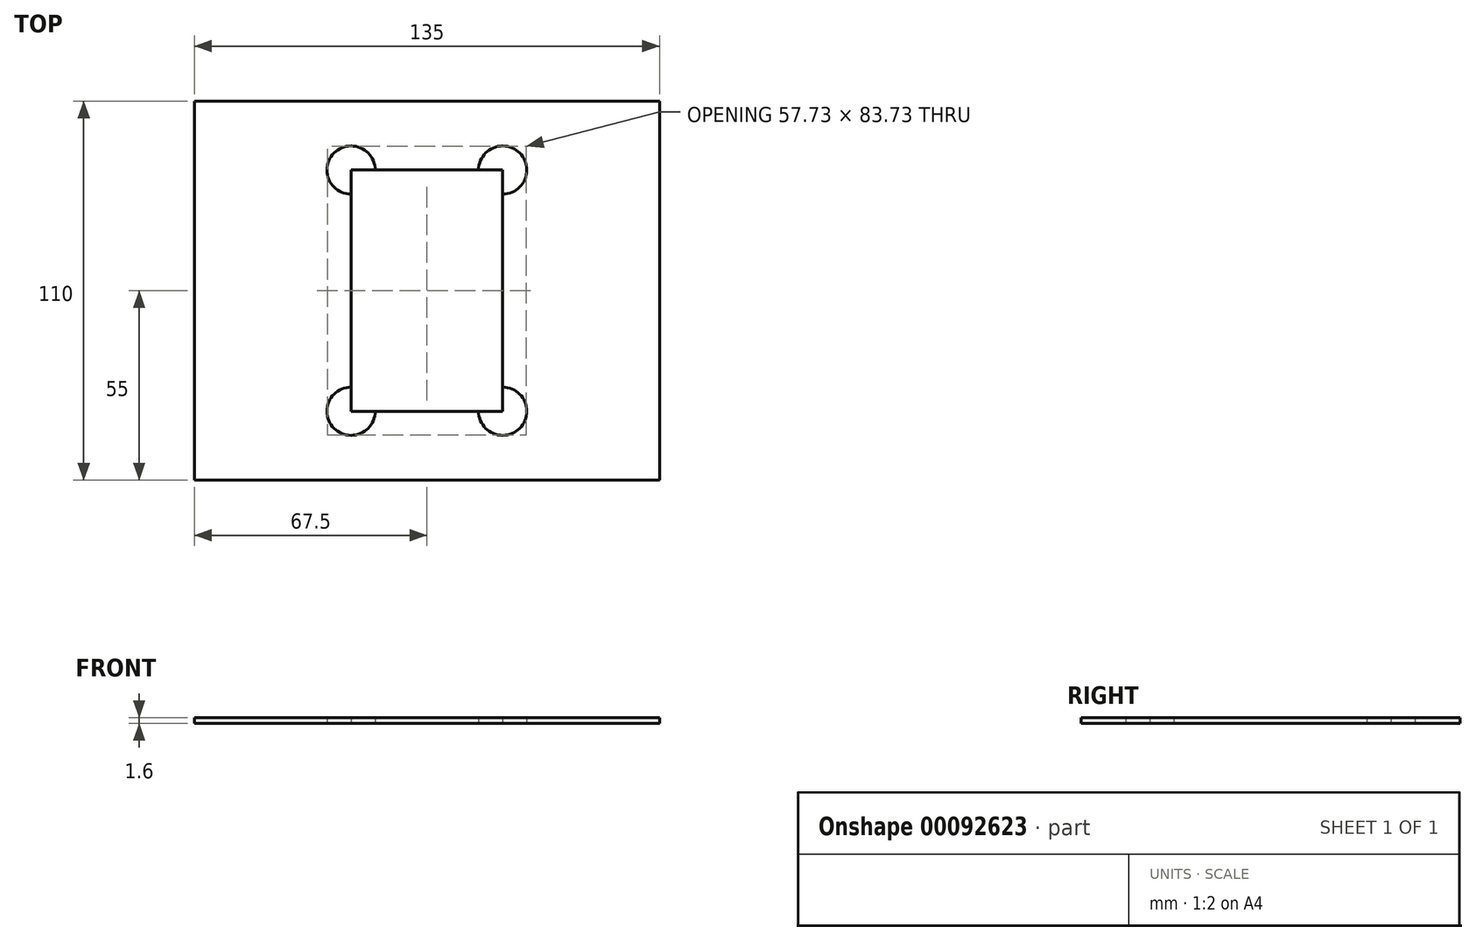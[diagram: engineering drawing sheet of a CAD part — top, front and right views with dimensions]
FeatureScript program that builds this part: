
annotation { "Feature Type Name" : "Feature", "Feature Type Description" : "" }
export const myFeature = defineFeature(function(context is Context, id is Id, definition is map)
    precondition{}
    {
        {
            var Q0;
            Q0=qCreatedBy(makeId("Top.planeOp"),FACE);
            var sketch = newSketch(context, id + "F0", { "sketchPlane" : qUnion([Q0])});
            skLineSegment(sketch, "E0.bottom", {"start": v(-22, 35) * mm, "end": v(22, 35) * mm});
            skLineSegment(sketch, "E0.top", {"start": v(-22, -35) * mm, "end": v(22, -35) * mm});
            skLineSegment(sketch, "E0.left", {"start": v(-22, 35) * mm, "end": v(-22, -35) * mm});
            skLineSegment(sketch, "E0.right", {"start": v(22, 35) * mm, "end": v(22, -35) * mm});
            skSolve(sketch);
        }
        {
            var Q0;
            Q0 = qSketchRegion(id + "F0", true);
            extrude(context, id + "F1", {"entities" : qUnion([Q0]), "depth" : 1.6 * mm, "offsetDistance" : 25 * mm});
        }
        {
            var Q0;
            Q0=qCreatedBy(makeId("Top.planeOp"),FACE);
            var sketch = newSketch(context, id + "F2", { "sketchPlane" : qUnion([Q0])});
            skLineSegment(sketch, "E1.bottom", {"start": v(-67.5, 55) * mm, "end": v(67.5, 55) * mm});
            skLineSegment(sketch, "E1.top", {"start": v(-67.5, -55) * mm, "end": v(67.5, -55) * mm});
            skLineSegment(sketch, "E1.left", {"start": v(-67.5, 55) * mm, "end": v(-67.5, -55) * mm});
            skLineSegment(sketch, "E1.right", {"start": v(67.5, 55) * mm, "end": v(67.5, -55) * mm});
            skLineSegment(sketch, "E2.0", {"start": v(-22, 28) * mm, "end": v(-22, -28) * mm});
            skLineSegment(sketch, "E2.1", {"start": v(-15, 35) * mm, "end": v(15, 35) * mm});
            skLineSegment(sketch, "E2.2", {"start": v(22, 28) * mm, "end": v(22, -28) * mm});
            skLineSegment(sketch, "E2.3", {"start": v(-15, -35) * mm, "end": v(15, -35) * mm});
            skArc(sketch, "E3", {"start": v(-15, 35) * mm, "mid": v(-26.95, 39.95) * mm, "end": v(-22, 28) * mm});
            skArc(sketch, "E4.MirrorCS", {"start": v(15, 35) * mm, "mid": v(26.95, 39.95) * mm, "end": v(22, 28) * mm});
            skArc(sketch, "E5.MirrorCS", {"start": v(15, -35) * mm, "mid": v(26.95, -39.95) * mm, "end": v(22, -28) * mm});
            skArc(sketch, "E6.MirrorCS", {"start": v(-15, -35) * mm, "mid": v(-26.95, -39.95) * mm, "end": v(-22, -28) * mm});
            skSolve(sketch);
        }
        {
            var Q0;
            Q0 = qSketchRegion(id + "F2", true);
            extrude(context, id + "F3", {"entities" : qUnion([Q0]), "depth" : 1.6 * mm, "offsetDistance" : 25 * mm});
        }
    });
